FCSTD DOCUMENT  (FreeCAD 0.15R4671 (Git))
Label: Tank Case
License: All rights reserved
LicenseURL: http://en.wikipedia.org/wiki/All_rights_reserved
objects: Sketcher::SketchObject×1
note: 1 computed .brp shape members not serialized (recipe doc carries the construction recipe); baked Part::Feature solids carry a one-line shape summary decoded from their .brp

FEATURE [Sketcher::SketchObject] Sketch
  sketch-geometry (15):
    g0: LineSegment StartX=-13.6643 StartY=6.03911 StartZ=0 EndX=-13.6506 EndY=3.95614 EndZ=0
    g1: LineSegment StartX=-13.6506 StartY=3.95614 StartZ=0 EndX=13.6506 EndY=3.95614 EndZ=0
    g2: LineSegment StartX=13.6506 StartY=3.95614 StartZ=0 EndX=13.6506 EndY=3.72616 EndZ=0
    g3: LineSegment StartX=13.6506 StartY=3.72616 StartZ=0 EndX=14.0048 EndY=6.00438 EndZ=0
    g4: LineSegment StartX=14.0048 StartY=6.00438 StartZ=0 EndX=16 EndY=7.3355 EndZ=0
    g5: LineSegment StartX=16 StartY=7.3355 StartZ=0 EndX=16 EndY=-30.6645 EndZ=0
    g6: LineSegment StartX=16 StartY=-30.6645 StartZ=0 EndX=16.1402 EndY=-28.2701 EndZ=0
    g7: LineSegment StartX=16.1402 StartY=-28.2701 StartZ=0 EndX=13.6506 EndY=-28.2701 EndZ=0
    g8: LineSegment StartX=13.6506 StartY=-28.2701 StartZ=0 EndX=13.6506 EndY=-28.5001 EndZ=0
    g9: LineSegment StartX=13.6506 StartY=-28.5001 StartZ=0 EndX=-13.6506 EndY=-28.5001 EndZ=0
    g10: LineSegment StartX=-13.6506 StartY=-28.5001 StartZ=0 EndX=-13.6506 EndY=-28.2701 EndZ=0
    g11: LineSegment StartX=-13.6506 StartY=-28.2701 StartZ=0 EndX=-16.1402 EndY=-28.2701 EndZ=0
    g12: LineSegment StartX=-16.1402 StartY=-28.2701 StartZ=0 EndX=-16 EndY=-30.6645 EndZ=0
    g13: LineSegment StartX=-16 StartY=-30.6645 StartZ=0 EndX=-16 EndY=7.3355 EndZ=0
    g14: ArcOfCircle CenterX=-18.1669 CenterY=0.679324 CenterZ=0 NormalX=0 NormalY=0 NormalZ=1 Radius=7 StartAngle=0.872103 EndAngle=1.25608
  constraints (36):
    c: Coincident(g1,g2)
    c: Coincident(g2,g3)
    c: Coincident(g3,g4)
    c: Coincident(g4,g5)
    c: Vertical(g5)
    c: Coincident(g5,g6)
    c: Coincident(g6,g7)
    c: Horizontal(g7)
    c: Coincident(g7,g8)
    c: Vertical(g8)
    c: Coincident(g8,g9)
    c: Horizontal(g9)
    c: Coincident(g9,g10)
    c: Coincident(g10,g11)
    c: Coincident(g11,g12)
    c: Coincident(g12,g13)
    c: Vertical(g13)
    c: Vertical(g10)
    c: Vertical(g2)
    c: Symmetric(g1,g1,g-2)
    c: Symmetric(g13,g4,g-2)
    c: Equal(g9,g1)
    c: Equal(g2,g8)
    c: Equal(g8,g10)
    c: Horizontal(g11)
    c: Equal(g11,g7)
    c: Equal(g4,g6)
    c: Equal(g6,g12)
    c: Equal(g13,g5)
    c: DistanceY(g13) = 38
    c: DistanceX(g13,g4) = 32
    c: Coincident(g14,g13)
    c: Coincident(g14,g0)
    c: Angle(g14) = 0.383972
    c: Radius(g14) = 7
    c: Coincident(g0,g1)
